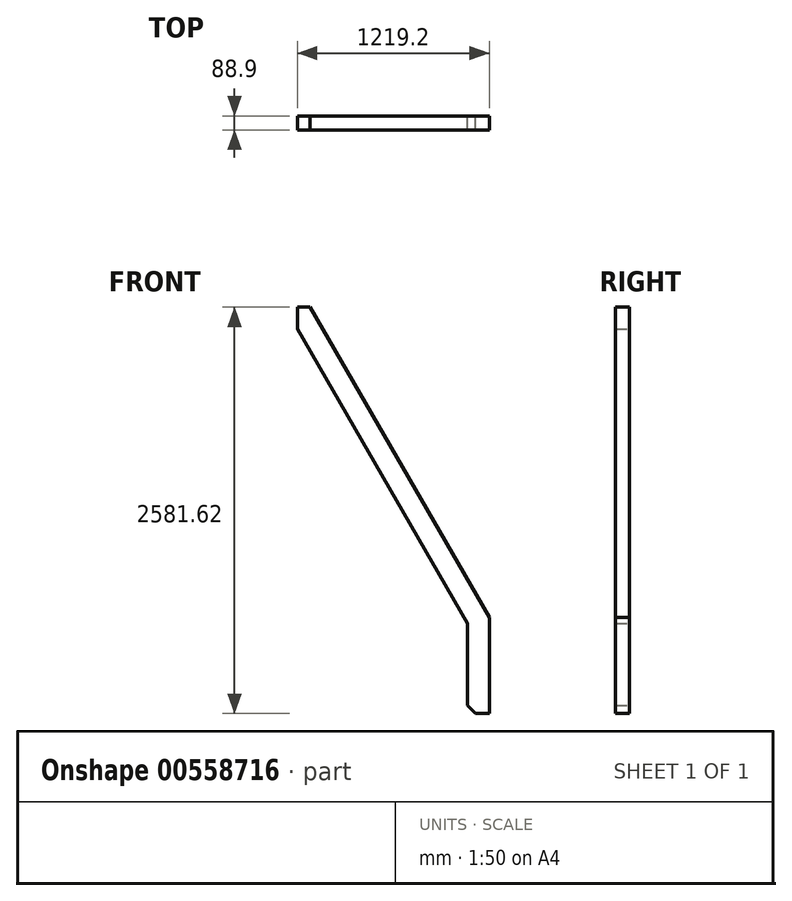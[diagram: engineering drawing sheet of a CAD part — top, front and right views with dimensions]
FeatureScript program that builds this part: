
annotation { "Feature Type Name" : "Feature", "Feature Type Description" : "" }
export const myFeature = defineFeature(function(context is Context, id is Id, definition is map)
    precondition{}
    {
        {
            var Q0;
            Q0=qCreatedBy(makeId("Front.planeOp"),FACE);
            var sketch = newSketch(context, id + "F0", { "sketchPlane" : qUnion([Q0])});
            skLineSegment(sketch, "E0", {"start": v(0, 0) * mm, "end": v(0, 609.6) * mm});
            skLineSegment(sketch, "E1", {"start": v(-139.7, 572.17) * mm, "end": v(-139.7, 50.8) * mm});
            skLineSegment(sketch, "E2", {"start": v(-139.7, 50.8) * mm, "end": v(-88.9, 0) * mm});
            skLineSegment(sketch, "E3", {"start": v(-88.9, 0) * mm, "end": v(0, 0) * mm});
            skLineSegment(sketch, "E4", {"start": v(0, 609.6) * mm, "end": v(-1138.54, 2581.62) * mm});
            skLineSegment(sketch, "E5", {"start": v(-139.7, 572.17) * mm, "end": v(-1219.2, 2441.92) * mm});
            skLineSegment(sketch, "E6", {"start": v(-1219.2, 2441.92) * mm, "end": v(-1219.2, 2581.62) * mm});
            skLineSegment(sketch, "E7", {"start": v(-1219.2, 2581.62) * mm, "end": v(-1138.54, 2581.62) * mm});
            skSolve(sketch);
        }
        {
            var Q0;
            Q0 = qSketchRegion(id + "F0", true);
            extrude(context, id + "F1", {"entities" : qUnion([Q0]), "depth" : 88.9 * mm, "offsetDistance" : 25.4 * mm});
        }
    });
